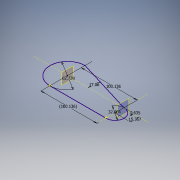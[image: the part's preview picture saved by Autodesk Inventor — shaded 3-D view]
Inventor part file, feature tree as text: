
AUTODESK INVENTOR PART (.ipt)
format: ipt  version: 2016 (Build 200138000, 138)  size: 105,984 bytes
history: native  units: mm
features: other x38, pattern_linear x2, plane x1, sketch x1
ambient origin geometry x8: Origin, YZ Plane, XZ Plane, XY Plane, X Axis, Y Axis, Z Axis, Center Point
feature tree (42):
  plane  "Work Plane1"
  sketch  "Sketch1"  dims[d0=100.136mm d1=62.738mm d2=32.004mm d3=100.136mm d4=15.367mm d5=2.977956mm d6=0.635mm d7=100.136mm d8=20.0mm d10=100.136mm d11=370.0mm]
  other  "Work Point1"
  pattern_linear  "Rectangular Pattern1"  Spacing1=62.738mm  [1 undecoded]
  pattern_linear  "Rectangular Pattern2"  Spacing1=32.004mm  [1 undecoded]
  other  "Work Point2"
  other  "Work Point3"
  other  "Work Point4"
  other  "Work Point5"
  other  "Work Point6"
  other  "Work Point7"
  other  "Work Point8"
  other  "Work Point9"
  other  "Work Point10"
  other  "Work Point11"
  other  "Work Point12"
  other  "Work Point13"
  other  "Work Point14"
  other  "Work Point15"
  other  "Work Point16"
  other  "Work Point17"
  other  "Work Point34"
  other  "Work Point35"
  other  "Work Point36"
  other  "Work Point37"
  other  "Work Point38"
  other  "Work Point39"
  other  "Work Point40"
  other  "Work Point41"
  other  "Work Point42"
  other  "Work Point43"
  other  "Work Point44"
  other  "Work Point45"
  other  "Work Point46"
  other  "Work Point47"
  other  "Work Point48"
  other  "Work Point50"
  other  "Work Point51"
  other  "Work Point52"
  other  "Work Point54"
  other  "Work Point58"
  other  "Work Point59"
note: 2 required parameter values undecoded (feature->parameter linkage not recoverable at this tier; creation-order binding heuristic only, values carry confidence <= 0.55)
